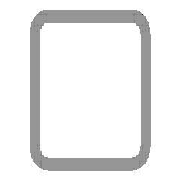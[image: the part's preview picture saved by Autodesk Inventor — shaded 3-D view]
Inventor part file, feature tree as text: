
AUTODESK INVENTOR PART (.ipt)
format: ipt  version: 2025 (Build 290162010, 162A)  size: 134,656 bytes
history: native  units: mm (DEFAULTED — no unit token found)
features: other x4, sketch x1, plane x1
ambient origin geometry x8: Origin, YZ Plane, XZ Plane, XY Plane, X Axis, Y Axis, Z Axis, Center Point
bodies: Solid1 (feature_tree), Body (feature_tree)
feature tree (6):
  parser-record x1  (decoder bookkeeping rows leaked as tree rows — omitted from the tree; the rows remain in map.json)
  other  "Driven Length"
  other  "Start Plane"
  other  "End Plane"
  sketch  "Sketch3"  dims[d3=1257.974796mm d4=0.0mm d7=6.0mm d9=80.0mm d11=80.0mm d12=3.0mm d13=40.0mm d14=1297.974796mm d15=40.0mm d16=40.0mm d17=90.0deg d18=1257.974796mm]
  plane  "Work Plane3"
